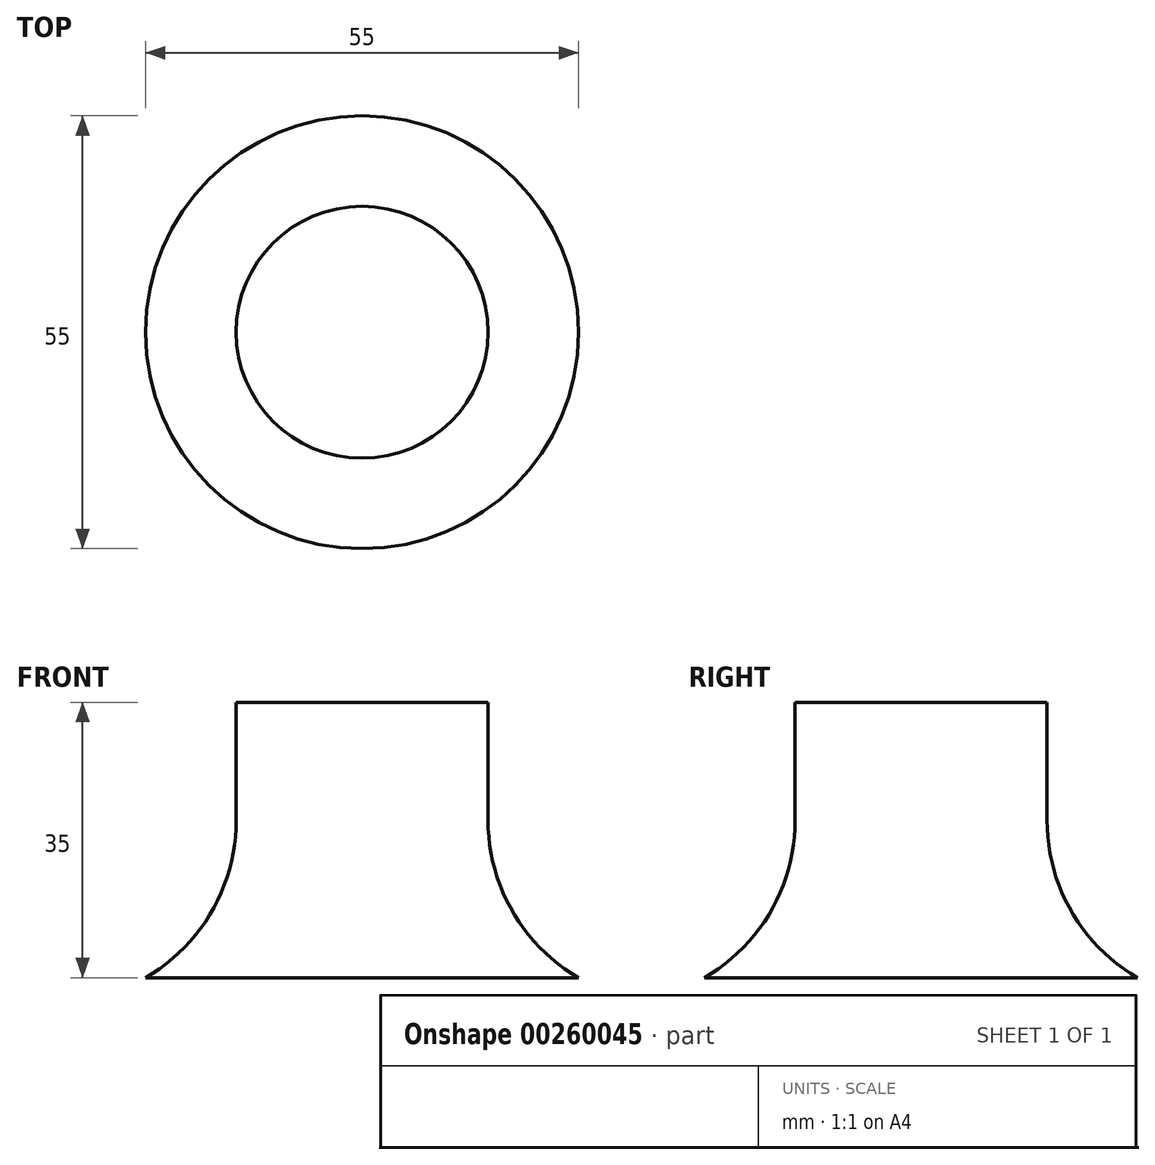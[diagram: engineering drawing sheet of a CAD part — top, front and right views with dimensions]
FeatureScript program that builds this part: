
annotation { "Feature Type Name" : "Feature", "Feature Type Description" : "" }
export const myFeature = defineFeature(function(context is Context, id is Id, definition is map)
    precondition{}
    {
        {
            var Q0;
            Q0=qCreatedBy(makeId("Front.planeOp"),FACE);
            var sketch = newSketch(context, id + "F0", { "sketchPlane" : qUnion([Q0])});
            skLineSegment(sketch, "E0", {"start": v(-27.5, 0) * mm, "end": v(0, 0) * mm});
            skLineSegment(sketch, "E1", {"start": v(0, 0) * mm, "end": v(0, 35) * mm});
            skLineSegment(sketch, "E2", {"start": v(0, 35) * mm, "end": v(-16, 35) * mm});
            skLineSegment(sketch, "E3", {"start": v(-16, 35) * mm, "end": v(-16, 20) * mm});
            skArc(sketch, "E4", {"start": v(-27.5, 0) * mm, "mid": v(-19.08, 8.46) * mm, "end": v(-16, 20) * mm});
            skLineSegment(sketch, "E5", {"start": v(0, 35) * mm, "end": v(16, 35) * mm, "construction": true});
            skLineSegment(sketch, "E6", {"start": v(0, 0) * mm, "end": v(27.5, 0) * mm, "construction": true});
            skSolve(sketch);
        }
        {
            var Q0;
            Q0 = qSketchRegion(id + "F0", true);
            var Q1;
            Q1=sQuery(id+"F0.wireOp",EDGE,"E1");
            revolve(context, id + "F1", {"entities" : qUnion([Q0]), "axis" : qUnion([Q1]), "revolveType" : RevolveType.FULL});
        }
    });
